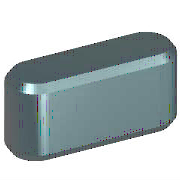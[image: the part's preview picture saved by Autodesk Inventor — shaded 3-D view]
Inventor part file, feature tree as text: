
AUTODESK INVENTOR PART (.ipt)
format: ipt  version: 2015 (Build 190159000, 159)  size: 135,680 bytes
history: native  units: mm (DEFAULTED — no unit token found)
features: plane x3, extrude x1
ambient origin geometry x8: Origin, YZ Plane, XZ Plane, XY Plane, X Axis, Y Axis, Z Axis, Center Point
bodies: Solid1 (feature_tree)
feature tree (4):
  plane  "Work Plane1"
  plane  "Work Plane2"
  extrude  "轴承体1"  Depth=4.0mm
  plane  "Work Plane3"
